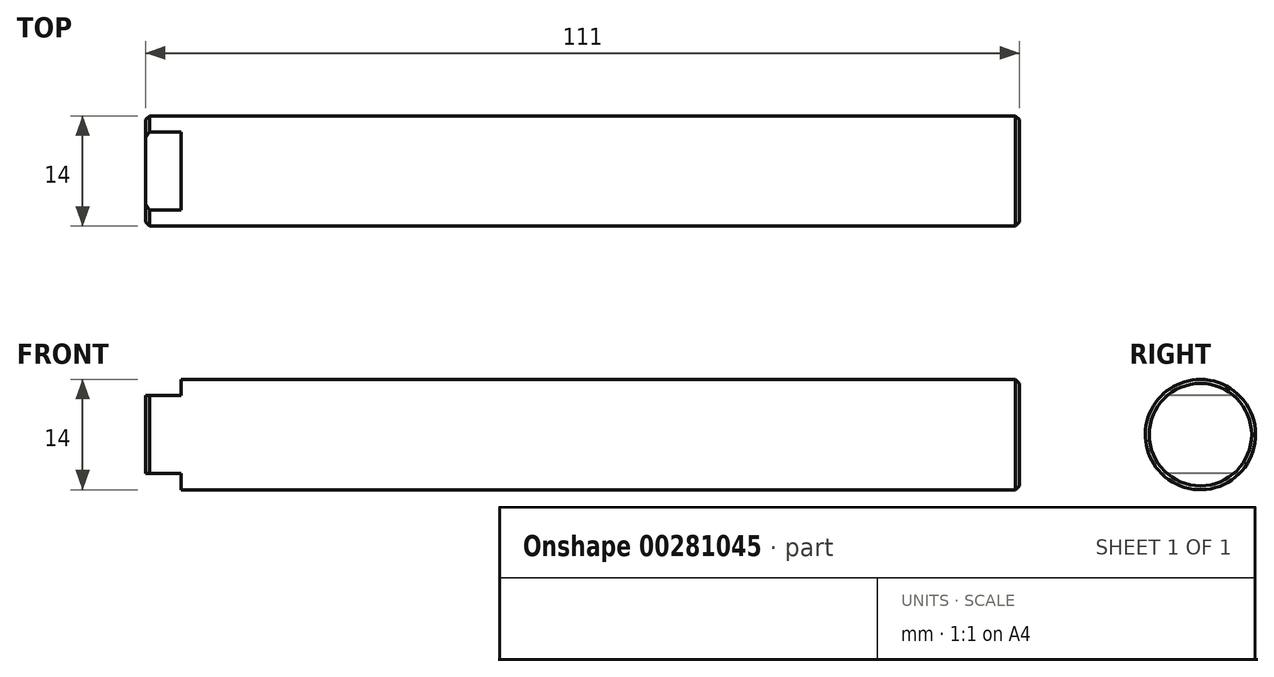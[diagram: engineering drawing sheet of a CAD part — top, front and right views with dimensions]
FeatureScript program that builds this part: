
annotation { "Feature Type Name" : "Feature", "Feature Type Description" : "" }
export const myFeature = defineFeature(function(context is Context, id is Id, definition is map)
    precondition{}
    {
        {
            var Q0;
            Q0=qCreatedBy(makeId("Front.planeOp"),FACE);
            var sketch = newSketch(context, id + "F0", { "sketchPlane" : qUnion([Q0])});
            skLineSegment(sketch, "E0", {"start": v(0, 0) * mm, "end": v(0, 7) * mm});
            skLineSegment(sketch, "E1", {"start": v(0, 7) * mm, "end": v(111, 7) * mm});
            skLineSegment(sketch, "E2", {"start": v(111, 7) * mm, "end": v(111, 0) * mm});
            skLineSegment(sketch, "E3", {"start": v(111, 0) * mm, "end": v(0, 0) * mm});
            skSolve(sketch);
        }
        {
            var Q0;
            Q0=makeQuery(id+"F0.imprint","IMPRINT",FACE,{"disambiguationData":[TD([[makeQuery(id+"F0.imprint","IMPRINT",EDGE,{"derivedFrom":sQuery(id+"F0.wireOp",EDGE,"E0")}),-1.0]])]});
            var Q1;
            Q1=sQuery(id+"F0.wireOp",EDGE,"E3");
            revolve(context, id + "F1", {"entities" : qUnion([Q0]), "axis" : qUnion([Q1]), "revolveType" : RevolveType.FULL});
        }
        {
            var Q0;
            Q0=qCreatedBy(makeId("Front.planeOp"),FACE);
            var sketch = newSketch(context, id + "F2", { "sketchPlane" : qUnion([Q0])});
            skLineSegment(sketch, "E4.bottom", {"start": v(0, 7) * mm, "end": v(4.5, 7) * mm});
            skLineSegment(sketch, "E4.top", {"start": v(0, 4.95) * mm, "end": v(4.5, 4.95) * mm});
            skLineSegment(sketch, "E4.left", {"start": v(0, 7) * mm, "end": v(0, 4.95) * mm});
            skLineSegment(sketch, "E4.right", {"start": v(4.5, 7) * mm, "end": v(4.5, 4.95) * mm});
            skLineSegment(sketch, "E5.MirrorCS", {"start": v(0, -7) * mm, "end": v(4.5, -7) * mm});
            skLineSegment(sketch, "E6.MirrorCS", {"start": v(0, -4.95) * mm, "end": v(4.5, -4.95) * mm});
            skLineSegment(sketch, "E7.MirrorCS", {"start": v(4.5, -7) * mm, "end": v(4.5, -4.95) * mm});
            skLineSegment(sketch, "E8.MirrorCS", {"start": v(0, -7) * mm, "end": v(0, -4.95) * mm});
            skSolve(sketch);
        }
        {
            var Q0;
            Q0 = qSketchRegion(id + "F2", true);
            extrude(context, id + "F3", {"entities" : qUnion([Q0]), "operationType" : NewBodyOperationType.REMOVE, "endBound" : BoundingType.SYMMETRIC, "oppositeDirection" : true, "depth" : 25 * mm});
        }
        {
            var Q0;
            Q0=makeQuery(id+"F3.boolean.opBoolean","SPLIT",EDGE,{"disambiguationData":[OD(0.0)],"derivedFrom":makeQuery(id+"F1.opRevolve","SWEPT_EDGE",EDGE,{"disambiguationData":[OSD([sQuery(id+"F0.wireOp",EDGE,"E0"),sQuery(id+"F0.wireOp",EDGE,"E1")])]})});
            var Q1;
            Q1=makeQuery(id+"F3.boolean.opBoolean","SPLIT",EDGE,{"disambiguationData":[OD(1.0)],"derivedFrom":makeQuery(id+"F1.opRevolve","SWEPT_EDGE",EDGE,{"disambiguationData":[OSD([sQuery(id+"F0.wireOp",EDGE,"E0"),sQuery(id+"F0.wireOp",EDGE,"E1")])]})});
            var Q2;
            Q2=makeQuery(id+"F1.opRevolve","SWEPT_EDGE",EDGE,{"disambiguationData":[OSD([sQuery(id+"F0.wireOp",EDGE,"E1"),sQuery(id+"F0.wireOp",EDGE,"E2")])]});
            chamfer(context, id + "F4", {"entities" : qUnion([Q0, Q1, Q2]), "width" : 0.5 * mm, "tangentPropagation" : true});
        }
    });
